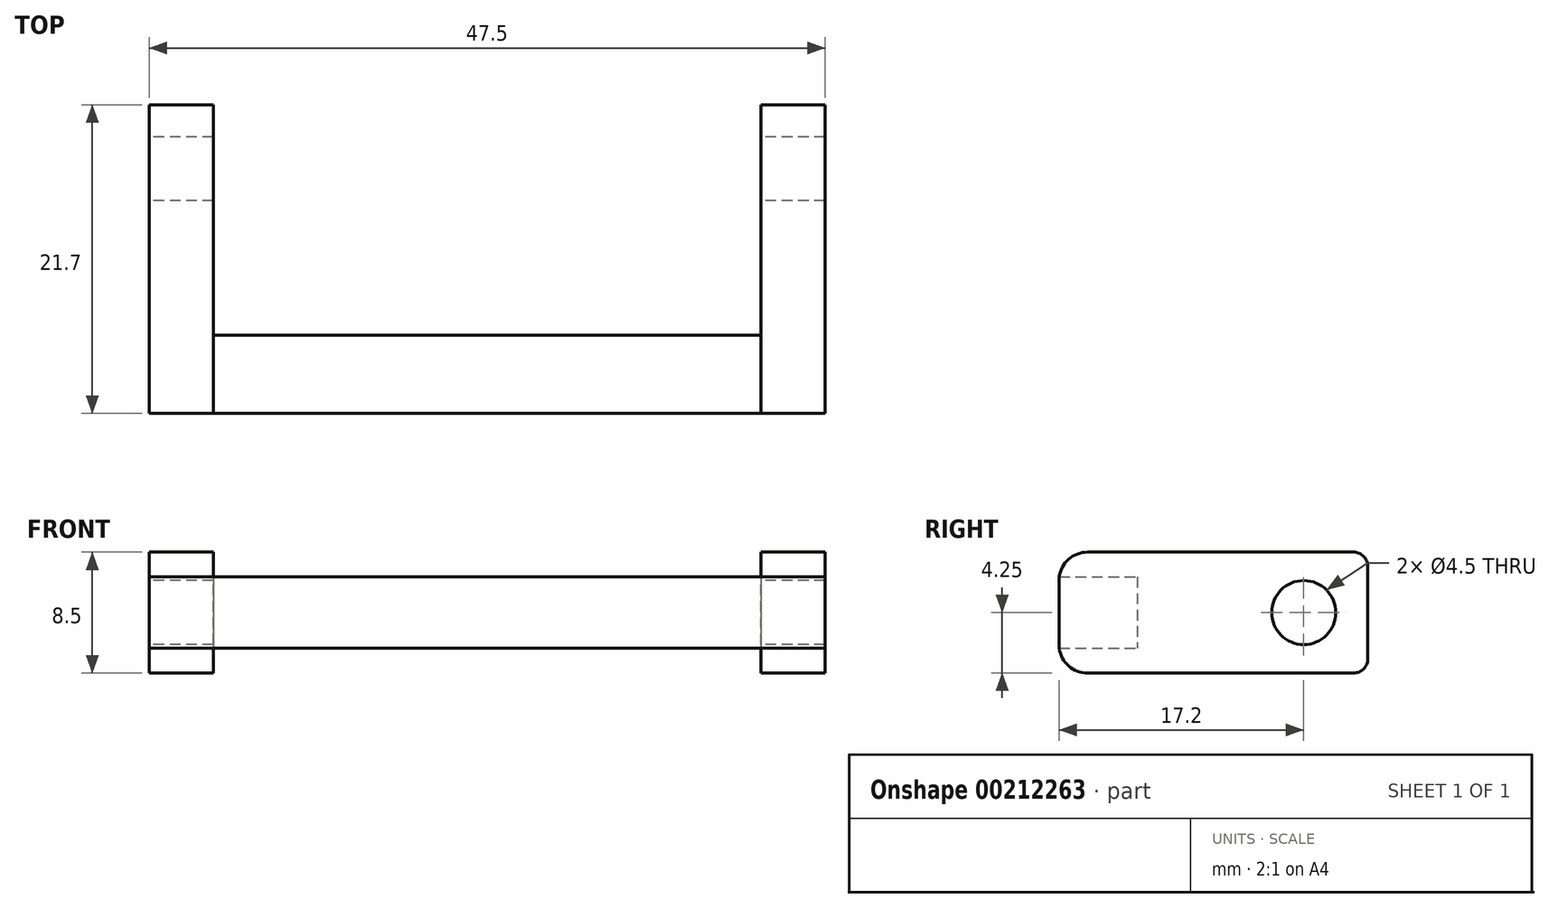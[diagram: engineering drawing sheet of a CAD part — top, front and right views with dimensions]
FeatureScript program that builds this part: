
annotation { "Feature Type Name" : "Feature", "Feature Type Description" : "" }
export const myFeature = defineFeature(function(context is Context, id is Id, definition is map)
    precondition{}
    {
        {
            var Q0;
            Q0=qCreatedBy(makeId("Top.planeOp"),FACE);
            var sketch = newSketch(context, id + "F0", { "sketchPlane" : qUnion([Q0])});
            skLineSegment(sketch, "E0.bottom", {"start": v(0, 0) * mm, "end": v(43, 0) * mm});
            skLineSegment(sketch, "E0.top", {"start": v(0, 5.5) * mm, "end": v(43, 5.5) * mm});
            skLineSegment(sketch, "E0.left", {"start": v(0, 0) * mm, "end": v(0, 5.5) * mm});
            skLineSegment(sketch, "E0.right", {"start": v(43, 0) * mm, "end": v(43, 5.5) * mm});
            skSolve(sketch);
        }
        {
            var Q0;
            Q0=makeQuery(id+"F0.imprint","IMPRINT",FACE,{"disambiguationData":[TD([[makeQuery(id+"F0.imprint","IMPRINT",EDGE,{"derivedFrom":sQuery(id+"F0.wireOp",EDGE,"E0.bottom")}),1.0]])]});
            extrude(context, id + "F1", {"entities" : qUnion([Q0]), "depth" : 5 * mm});
        }
        {
            var Q0;
            Q0=qCreatedBy(makeId("Right.planeOp"),FACE);
            var sketch = newSketch(context, id + "F2", { "sketchPlane" : qUnion([Q0])});
            skLineSegment(sketch, "E1.bottom", {"start": v(2, -1.75) * mm, "end": v(20.7, -1.75) * mm});
            skLineSegment(sketch, "E1.top", {"start": v(2, 6.75) * mm, "end": v(20.7, 6.75) * mm});
            skLineSegment(sketch, "E1.left", {"start": v(0, 4.75) * mm, "end": v(0, 0.25) * mm});
            skLineSegment(sketch, "E1.right", {"start": v(21.7, 5.75) * mm, "end": v(21.7, -0.75) * mm});
            skLineSegment(sketch, "E2", {"start": v(21.7, 2.5) * mm, "end": v(0, 2.5) * mm, "construction": true});
            skPoint(sketch, "E3.visualSharp", {"position": v(0, -1.75) * mm});
            skArc(sketch, "E3.filletArc", {"start": v(0, 0.25) * mm, "mid": v(0.59, -1.16) * mm, "end": v(2, -1.75) * mm});
            skPoint(sketch, "E4.visualSharp", {"position": v(0, 6.75) * mm});
            skArc(sketch, "E4.filletArc", {"start": v(2, 6.75) * mm, "mid": v(0.59, 6.16) * mm, "end": v(0, 4.75) * mm});
            skPoint(sketch, "E5.visualSharp", {"position": v(21.7, -1.75) * mm});
            skArc(sketch, "E5.filletArc", {"start": v(20.7, -1.75) * mm, "mid": v(21.4, -1.46) * mm, "end": v(21.7, -0.75) * mm});
            skPoint(sketch, "E6.visualSharp", {"position": v(21.7, 6.75) * mm});
            skArc(sketch, "E6.filletArc", {"start": v(21.7, 5.75) * mm, "mid": v(21.4, 6.46) * mm, "end": v(20.7, 6.75) * mm});
            skSolve(sketch);
        }
        {
            var Q0;
            Q0 = qSketchRegion(id + "F2", true);
            extrude(context, id + "F3", {"entities" : qUnion([Q0]), "operationType" : NewBodyOperationType.ADD, "depth" : 4.5 * mm});
        }
        {
            var Q0;
            Q0=makeQuery(id+"F1.opExtrude","SWEPT_FACE",FACE,{"disambiguationData":[OSD([sQuery(id+"F0.wireOp",EDGE,"E0.right")])]});
            var sketch = newSketch(context, id + "F4", { "sketchPlane" : qUnion([Q0])});
            skLineSegment(sketch, "E7.0.0", {"start": v(0, 5) * mm, "end": v(0.02, 5) * mm});
            skArc(sketch, "E7.0.1", {"start": v(0.02, 5) * mm, "mid": v(0.68, 6.25) * mm, "end": v(2, 6.75) * mm});
            skLineSegment(sketch, "E7.0.2", {"start": v(2, 6.75) * mm, "end": v(20.7, 6.75) * mm});
            skArc(sketch, "E7.0.3", {"start": v(20.7, 6.75) * mm, "mid": v(21.4, 6.46) * mm, "end": v(21.7, 5.75) * mm});
            skLineSegment(sketch, "E7.0.4", {"start": v(21.7, 5.75) * mm, "end": v(21.7, -0.75) * mm});
            skArc(sketch, "E7.0.5", {"start": v(21.7, -0.75) * mm, "mid": v(21.4, -1.46) * mm, "end": v(20.7, -1.75) * mm});
            skLineSegment(sketch, "E7.0.6", {"start": v(20.7, -1.75) * mm, "end": v(2, -1.75) * mm});
            skArc(sketch, "E7.0.7", {"start": v(2, -1.75) * mm, "mid": v(0.68, -1.25) * mm, "end": v(0.02, 0) * mm});
            skLineSegment(sketch, "E7.0.8", {"start": v(0.02, 0) * mm, "end": v(0, 0) * mm});
            skLineSegment(sketch, "E7.0.9", {"start": v(0, 0) * mm, "end": v(0, 5) * mm});
            skSolve(sketch);
        }
        {
            var Q0;
            Q0 = qSketchRegion(id + "F4", true);
            extrude(context, id + "F5", {"entities" : qUnion([Q0]), "operationType" : NewBodyOperationType.ADD, "depth" : 4.5 * mm});
        }
        {
            var Q0;
            Q0=makeQuery(id+"F3.boolean.opBoolean","MERGE",FACE,{"derivedFrom":[makeQuery(id+"F1.opExtrude","SWEPT_FACE",FACE,{"disambiguationData":[OSD([sQuery(id+"F0.wireOp",EDGE,"E0.left")])]}),makeQuery(id+"F3.opExtrude","CAP_FACE",FACE,{"disambiguationData":[OSD([sQuery(id+"F2.wireOp",EDGE,"E1.bottom"),sQuery(id+"F2.wireOp",EDGE,"E1.top"),sQuery(id+"F2.wireOp",EDGE,"E1.left"),sQuery(id+"F2.wireOp",EDGE,"E1.right"),sQuery(id+"F2.wireOp",EDGE,"E3.filletArc"),sQuery(id+"F2.wireOp",EDGE,"E4.filletArc"),sQuery(id+"F2.wireOp",EDGE,"E5.filletArc"),sQuery(id+"F2.wireOp",EDGE,"E6.filletArc")])],"isStart":true})]});
            var sketch = newSketch(context, id + "F6", { "sketchPlane" : qUnion([Q0])});
            skCircle(sketch, "E8", {"center": v(-17.2, 2.5) * mm, "radius": 2.25 * mm});
            skPoint(sketch, "E8.centerSnap0", {"position": v(-21.7, 2.5) * mm});
            skSolve(sketch);
        }
        {
            var Q0;
            Q0 = qSketchRegion(id + "F6", true);
            extrude(context, id + "F7", {"entities" : qUnion([Q0]), "operationType" : NewBodyOperationType.REMOVE, "endBound" : BoundingType.THROUGH_ALL, "oppositeDirection" : true, "depth" : 25 * mm});
        }
    });
